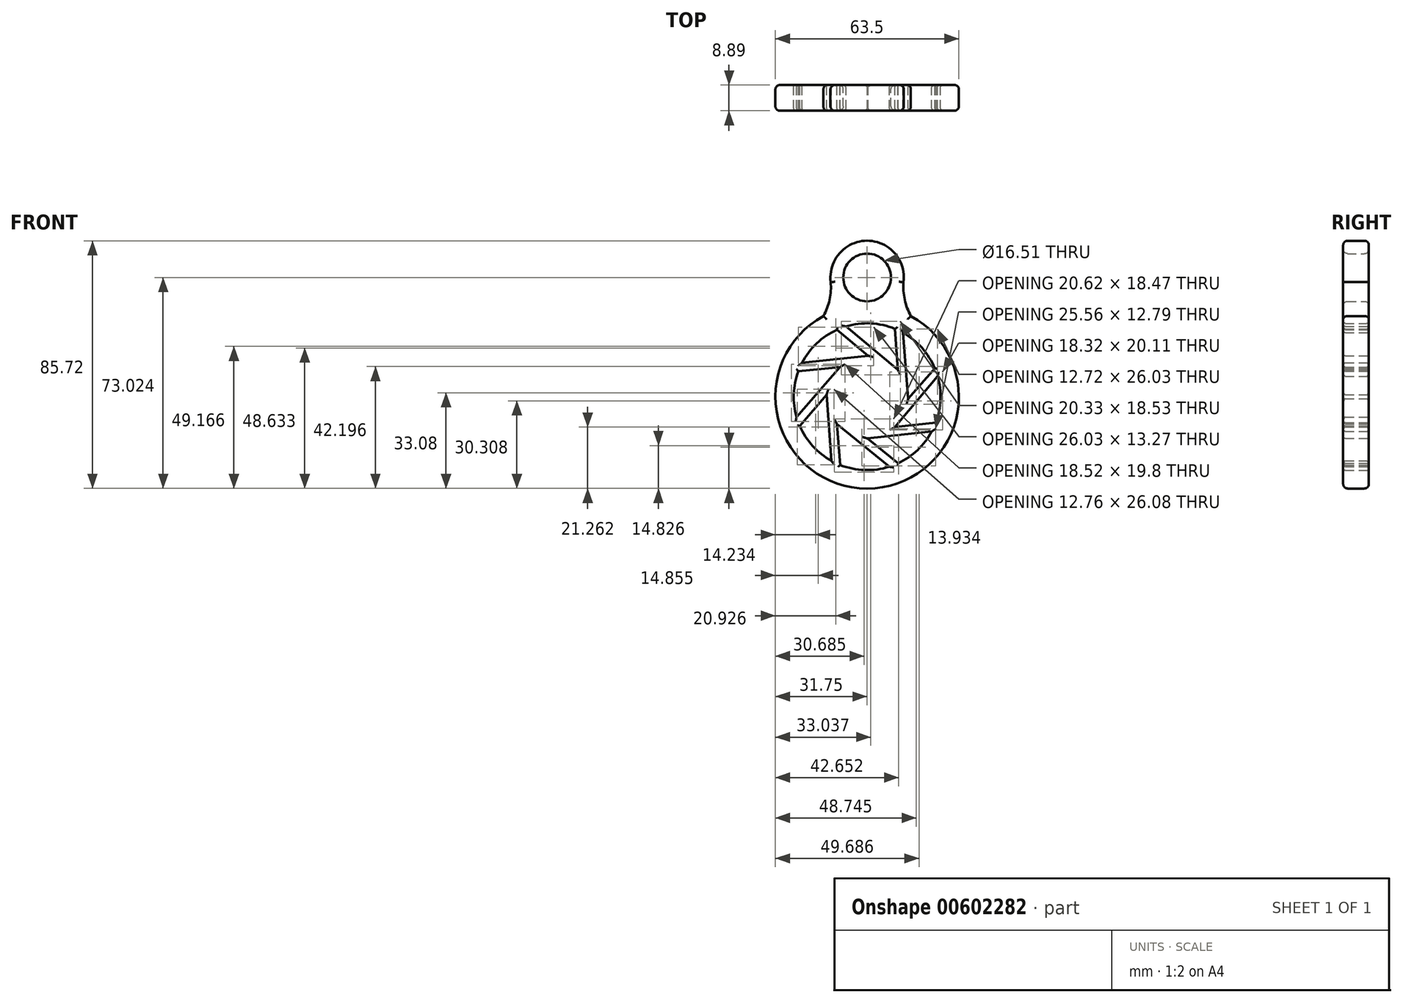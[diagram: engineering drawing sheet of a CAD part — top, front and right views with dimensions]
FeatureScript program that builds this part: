
annotation { "Feature Type Name" : "Feature", "Feature Type Description" : "" }
export const myFeature = defineFeature(function(context is Context, id is Id, definition is map)
    precondition{}
    {
        {
            var Q0;
            Q0=qCreatedBy(makeId("Front.planeOp"),FACE);
            var sketch = newSketch(context, id + "F0", { "sketchPlane" : qUnion([Q0])});
            skArc(sketch, "E0", {"start": v(-15.73, 48.69) * mm, "mid": v(-24.16, 50.57) * mm, "end": v(-32.74, 49.52) * mm});
            skLineSegment(sketch, "E1", {"start": v(-49.23, 34) * mm, "end": v(-34.86, 35.47) * mm});
            skLineSegment(sketch, "E2", {"start": v(-34.86, 35.47) * mm, "end": v(-49.8, 18.16) * mm});
            skLineSegment(sketch, "E3", {"start": v(-48.7, 15.1) * mm, "end": v(-39.45, 25.87) * mm});
            skLineSegment(sketch, "E4", {"start": v(-39.45, 25.87) * mm, "end": v(-37.7, 2.98) * mm});
            skLineSegment(sketch, "E5", {"start": v(-34.68, 1.56) * mm, "end": v(-35.87, 15.8) * mm});
            skLineSegment(sketch, "E6", {"start": v(-35.87, 15.8) * mm, "end": v(-17.7, 1) * mm});
            skLineSegment(sketch, "E7", {"start": v(-14.67, 2.18) * mm, "end": v(-25.36, 10.77) * mm});
            skLineSegment(sketch, "E8", {"start": v(-25.36, 10.77) * mm, "end": v(-3.03, 13.17) * mm});
            skLineSegment(sketch, "E9", {"start": v(-1.6, 16.3) * mm, "end": v(-15.75, 14.68) * mm});
            skLineSegment(sketch, "E10", {"start": v(-15.75, 14.68) * mm, "end": v(-1, 32.26) * mm});
            skLineSegment(sketch, "E11", {"start": v(-1.99, 35.05) * mm, "end": v(-11.16, 24.5) * mm});
            skLineSegment(sketch, "E12", {"start": v(-11.16, 24.5) * mm, "end": v(-12.95, 47.34) * mm});
            skLineSegment(sketch, "E13", {"start": v(-15.73, 48.69) * mm, "end": v(-14.82, 34.54) * mm});
            skLineSegment(sketch, "E14", {"start": v(-14.82, 34.54) * mm, "end": v(-32.74, 49.52) * mm});
            skLineSegment(sketch, "E15", {"start": v(-35.82, 48.36) * mm, "end": v(-25.08, 39.42) * mm});
            skLineSegment(sketch, "E16", {"start": v(-25.08, 39.42) * mm, "end": v(-47.95, 36.9) * mm});
            skArc(sketch, "E17", {"start": v(-40.52, 53.12) * mm, "mid": v(-25.4, -6.55) * mm, "end": v(-10.28, 53.12) * mm});
            skArc(sketch, "E18.trimOffspring", {"start": v(-35.82, 48.36) * mm, "mid": v(-42.85, 43.65) * mm, "end": v(-47.95, 36.9) * mm});
            skArc(sketch, "E19.trimOffspring", {"start": v(-49.23, 34) * mm, "mid": v(-50.78, 26.13) * mm, "end": v(-49.8, 18.16) * mm});
            skArc(sketch, "E20.trimOffspring", {"start": v(-48.7, 15.1) * mm, "mid": v(-44.2, 8.13) * mm, "end": v(-37.7, 2.98) * mm});
            skArc(sketch, "E21.trimOffspring", {"start": v(-34.68, 1.56) * mm, "mid": v(-26.24, -0.19) * mm, "end": v(-17.7, 1) * mm});
            skArc(sketch, "E22.trimOffspring", {"start": v(-14.67, 2.18) * mm, "mid": v(-7.96, 6.73) * mm, "end": v(-3.03, 13.17) * mm});
            skArc(sketch, "E23.trimOffspring", {"start": v(-1.6, 16.3) * mm, "mid": v(-0.02, 24.24) * mm, "end": v(-1, 32.26) * mm});
            skArc(sketch, "E24.trimOffspring", {"start": v(-1.99, 35.05) * mm, "mid": v(-6.45, 42.1) * mm, "end": v(-12.95, 47.34) * mm});
            skLineSegment(sketch, "E25", {"start": v(-25.4, 25.2) * mm, "end": v(-25.4, 76) * mm, "construction": true});
            skLineSegment(sketch, "E26", {"start": v(-25.4, 56.95) * mm, "end": v(-25.4, 76) * mm});
            skArc(sketch, "E27", {"start": v(-12.8, 64.84) * mm, "mid": v(-25.4, 79.17) * mm, "end": v(-38, 64.84) * mm});
            skArc(sketch, "E28", {"start": v(-40.52, 53.12) * mm, "mid": v(-38.4, 58.8) * mm, "end": v(-38, 64.84) * mm});
            skArc(sketch, "E29", {"start": v(-12.8, 64.84) * mm, "mid": v(-12.39, 58.8) * mm, "end": v(-10.28, 53.12) * mm});
            skCircle(sketch, "E30", {"center": v(-25.4, 66.47) * mm, "radius": 8.26 * mm});
            skSolve(sketch);
        }
        {
            var Q0;
            Q0=makeQuery(id+"F0.imprint","IMPRINT",FACE,{"disambiguationData":[TD([[makeQuery(id+"F0.imprint","IMPRINT",EDGE,{"derivedFrom":sQuery(id+"F0.wireOp",EDGE,"E0")}),-1.0]])]});
            extrude(context, id + "F1", {"entities" : qUnion([Q0]), "depth" : 8.9 * mm, "offsetDistance" : 25.4 * mm});
        }
        {
            var Q0;
            Q0=makeQuery(id+"F1.opExtrude","CAP_EDGE",EDGE,{"disambiguationData":[OSD([sQuery(id+"F0.wireOp",EDGE,"E17")])],"isStart":false});
            var Q1;
            Q1=makeQuery(id+"F1.opExtrude","CAP_EDGE",EDGE,{"disambiguationData":[OSD([sQuery(id+"F0.wireOp",EDGE,"E17")])],"isStart":true});
            var Q2;
            Q2=makeQuery(id+"F1.opExtrude","CAP_EDGE",EDGE,{"disambiguationData":[OSD([sQuery(id+"F0.wireOp",EDGE,"E29")])],"isStart":false});
            var Q3;
            Q3=makeQuery(id+"F1.opExtrude","CAP_EDGE",EDGE,{"disambiguationData":[OSD([sQuery(id+"F0.wireOp",EDGE,"E29")])],"isStart":true});
            var Q4;
            Q4=makeQuery(id+"F1.opExtrude","CAP_EDGE",EDGE,{"disambiguationData":[OSD([sQuery(id+"F0.wireOp",EDGE,"E28")])],"isStart":false});
            var Q5;
            Q5=makeQuery(id+"F1.opExtrude","CAP_EDGE",EDGE,{"disambiguationData":[OSD([sQuery(id+"F0.wireOp",EDGE,"E28")])],"isStart":true});
            var Q6;
            Q6=makeQuery(id+"F1.opExtrude","CAP_EDGE",EDGE,{"disambiguationData":[OSD([sQuery(id+"F0.wireOp",EDGE,"E27")])],"isStart":false});
            var Q7;
            Q7=makeQuery(id+"F1.opExtrude","CAP_EDGE",EDGE,{"disambiguationData":[OSD([sQuery(id+"F0.wireOp",EDGE,"E27")])],"isStart":true});
            var Q8;
            Q8=makeQuery(id+"F1.opExtrude","CAP_EDGE",EDGE,{"disambiguationData":[OSD([sQuery(id+"F0.wireOp",EDGE,"E30")])],"isStart":false});
            var Q9;
            Q9=makeQuery(id+"F1.opExtrude","CAP_EDGE",EDGE,{"disambiguationData":[OSD([sQuery(id+"F0.wireOp",EDGE,"E30")])],"isStart":true});
            fillet(context, id + "F2", {"entities" : qUnion([Q0, Q1, Q2, Q3, Q4, Q5, Q6, Q7, Q8, Q9]), "radius" : 1.52 * mm, "tangentPropagation" : true, "allowEdgeOverflow" : false});
        }
        {
            var Q0;
            Q0=makeQuery(id+"F1.opExtrude","CAP_EDGE",EDGE,{"disambiguationData":[OSD([sQuery(id+"F0.wireOp",EDGE,"E20.trimOffspring")])],"isStart":false});
            var Q1;
            Q1=makeQuery(id+"F1.opExtrude","CAP_EDGE",EDGE,{"disambiguationData":[OSD([sQuery(id+"F0.wireOp",EDGE,"E4")])],"isStart":false});
            var Q2;
            Q2=makeQuery(id+"F1.opExtrude","CAP_EDGE",EDGE,{"disambiguationData":[OSD([sQuery(id+"F0.wireOp",EDGE,"E3")])],"isStart":false});
            var Q3;
            Q3=makeQuery(id+"F1.opExtrude","CAP_EDGE",EDGE,{"disambiguationData":[OSD([sQuery(id+"F0.wireOp",EDGE,"E2")])],"isStart":false});
            var Q4;
            Q4=makeQuery(id+"F1.opExtrude","CAP_EDGE",EDGE,{"disambiguationData":[OSD([sQuery(id+"F0.wireOp",EDGE,"E19.trimOffspring")])],"isStart":false});
            var Q5;
            Q5=makeQuery(id+"F1.opExtrude","CAP_EDGE",EDGE,{"disambiguationData":[OSD([sQuery(id+"F0.wireOp",EDGE,"E1")])],"isStart":false});
            var Q6;
            Q6=makeQuery(id+"F1.opExtrude","CAP_EDGE",EDGE,{"disambiguationData":[OSD([sQuery(id+"F0.wireOp",EDGE,"E16")])],"isStart":false});
            var Q7;
            Q7=makeQuery(id+"F1.opExtrude","CAP_EDGE",EDGE,{"disambiguationData":[OSD([sQuery(id+"F0.wireOp",EDGE,"E18.trimOffspring")])],"isStart":false});
            var Q8;
            Q8=makeQuery(id+"F1.opExtrude","CAP_EDGE",EDGE,{"disambiguationData":[OSD([sQuery(id+"F0.wireOp",EDGE,"E15")])],"isStart":false});
            var Q9;
            Q9=makeQuery(id+"F1.opExtrude","CAP_EDGE",EDGE,{"disambiguationData":[OSD([sQuery(id+"F0.wireOp",EDGE,"E0")])],"isStart":false});
            var Q10;
            Q10=makeQuery(id+"F1.opExtrude","CAP_EDGE",EDGE,{"disambiguationData":[OSD([sQuery(id+"F0.wireOp",EDGE,"E14")])],"isStart":false});
            var Q11;
            Q11=makeQuery(id+"F1.opExtrude","CAP_EDGE",EDGE,{"disambiguationData":[OSD([sQuery(id+"F0.wireOp",EDGE,"E13")])],"isStart":false});
            var Q12;
            Q12=makeQuery(id+"F1.opExtrude","CAP_EDGE",EDGE,{"disambiguationData":[OSD([sQuery(id+"F0.wireOp",EDGE,"E12")])],"isStart":false});
            var Q13;
            Q13=makeQuery(id+"F1.opExtrude","CAP_EDGE",EDGE,{"disambiguationData":[OSD([sQuery(id+"F0.wireOp",EDGE,"E24.trimOffspring")])],"isStart":false});
            var Q14;
            Q14=makeQuery(id+"F1.opExtrude","CAP_EDGE",EDGE,{"disambiguationData":[OSD([sQuery(id+"F0.wireOp",EDGE,"E11")])],"isStart":false});
            var Q15;
            Q15=makeQuery(id+"F1.opExtrude","CAP_EDGE",EDGE,{"disambiguationData":[OSD([sQuery(id+"F0.wireOp",EDGE,"E10")])],"isStart":false});
            var Q16;
            Q16=makeQuery(id+"F1.opExtrude","CAP_EDGE",EDGE,{"disambiguationData":[OSD([sQuery(id+"F0.wireOp",EDGE,"E23.trimOffspring")])],"isStart":false});
            var Q17;
            Q17=makeQuery(id+"F1.opExtrude","CAP_EDGE",EDGE,{"disambiguationData":[OSD([sQuery(id+"F0.wireOp",EDGE,"E9")])],"isStart":false});
            var Q18;
            Q18=makeQuery(id+"F1.opExtrude","CAP_EDGE",EDGE,{"disambiguationData":[OSD([sQuery(id+"F0.wireOp",EDGE,"E8")])],"isStart":false});
            var Q19;
            Q19=makeQuery(id+"F1.opExtrude","CAP_EDGE",EDGE,{"disambiguationData":[OSD([sQuery(id+"F0.wireOp",EDGE,"E22.trimOffspring")])],"isStart":false});
            var Q20;
            Q20=makeQuery(id+"F1.opExtrude","CAP_EDGE",EDGE,{"disambiguationData":[OSD([sQuery(id+"F0.wireOp",EDGE,"E7")])],"isStart":false});
            var Q21;
            Q21=makeQuery(id+"F1.opExtrude","CAP_EDGE",EDGE,{"disambiguationData":[OSD([sQuery(id+"F0.wireOp",EDGE,"E21.trimOffspring")])],"isStart":false});
            var Q22;
            Q22=makeQuery(id+"F1.opExtrude","CAP_EDGE",EDGE,{"disambiguationData":[OSD([sQuery(id+"F0.wireOp",EDGE,"E6")])],"isStart":false});
            var Q23;
            Q23=makeQuery(id+"F1.opExtrude","CAP_EDGE",EDGE,{"disambiguationData":[OSD([sQuery(id+"F0.wireOp",EDGE,"E5")])],"isStart":false});
            var Q24;
            Q24=makeQuery(id+"F1.opExtrude","CAP_EDGE",EDGE,{"disambiguationData":[OSD([sQuery(id+"F0.wireOp",EDGE,"E14")])],"isStart":true});
            var Q25;
            Q25=makeQuery(id+"F1.opExtrude","CAP_EDGE",EDGE,{"disambiguationData":[OSD([sQuery(id+"F0.wireOp",EDGE,"E13")])],"isStart":true});
            var Q26;
            Q26=makeQuery(id+"F1.opExtrude","CAP_EDGE",EDGE,{"disambiguationData":[OSD([sQuery(id+"F0.wireOp",EDGE,"E0")])],"isStart":true});
            var Q27;
            Q27=makeQuery(id+"F1.opExtrude","CAP_EDGE",EDGE,{"disambiguationData":[OSD([sQuery(id+"F0.wireOp",EDGE,"E18.trimOffspring")])],"isStart":true});
            var Q28;
            Q28=makeQuery(id+"F1.opExtrude","CAP_EDGE",EDGE,{"disambiguationData":[OSD([sQuery(id+"F0.wireOp",EDGE,"E16")])],"isStart":true});
            var Q29;
            Q29=makeQuery(id+"F1.opExtrude","CAP_EDGE",EDGE,{"disambiguationData":[OSD([sQuery(id+"F0.wireOp",EDGE,"E15")])],"isStart":true});
            var Q30;
            Q30=makeQuery(id+"F1.opExtrude","CAP_EDGE",EDGE,{"disambiguationData":[OSD([sQuery(id+"F0.wireOp",EDGE,"E1")])],"isStart":true});
            var Q31;
            Q31=makeQuery(id+"F1.opExtrude","CAP_EDGE",EDGE,{"disambiguationData":[OSD([sQuery(id+"F0.wireOp",EDGE,"E2")])],"isStart":true});
            var Q32;
            Q32=makeQuery(id+"F1.opExtrude","CAP_EDGE",EDGE,{"disambiguationData":[OSD([sQuery(id+"F0.wireOp",EDGE,"E19.trimOffspring")])],"isStart":true});
            var Q33;
            Q33=makeQuery(id+"F1.opExtrude","CAP_EDGE",EDGE,{"disambiguationData":[OSD([sQuery(id+"F0.wireOp",EDGE,"E20.trimOffspring")])],"isStart":true});
            var Q34;
            Q34=makeQuery(id+"F1.opExtrude","CAP_EDGE",EDGE,{"disambiguationData":[OSD([sQuery(id+"F0.wireOp",EDGE,"E3")])],"isStart":true});
            var Q35;
            Q35=makeQuery(id+"F1.opExtrude","CAP_EDGE",EDGE,{"disambiguationData":[OSD([sQuery(id+"F0.wireOp",EDGE,"E4")])],"isStart":true});
            var Q36;
            Q36=makeQuery(id+"F1.opExtrude","CAP_EDGE",EDGE,{"disambiguationData":[OSD([sQuery(id+"F0.wireOp",EDGE,"E6")])],"isStart":true});
            var Q37;
            Q37=makeQuery(id+"F1.opExtrude","CAP_EDGE",EDGE,{"disambiguationData":[OSD([sQuery(id+"F0.wireOp",EDGE,"E5")])],"isStart":true});
            var Q38;
            Q38=makeQuery(id+"F1.opExtrude","CAP_EDGE",EDGE,{"disambiguationData":[OSD([sQuery(id+"F0.wireOp",EDGE,"E21.trimOffspring")])],"isStart":true});
            var Q39;
            Q39=makeQuery(id+"F1.opExtrude","CAP_EDGE",EDGE,{"disambiguationData":[OSD([sQuery(id+"F0.wireOp",EDGE,"E7")])],"isStart":true});
            var Q40;
            Q40=makeQuery(id+"F1.opExtrude","CAP_EDGE",EDGE,{"disambiguationData":[OSD([sQuery(id+"F0.wireOp",EDGE,"E8")])],"isStart":true});
            var Q41;
            Q41=makeQuery(id+"F1.opExtrude","CAP_EDGE",EDGE,{"disambiguationData":[OSD([sQuery(id+"F0.wireOp",EDGE,"E22.trimOffspring")])],"isStart":true});
            var Q42;
            Q42=makeQuery(id+"F1.opExtrude","CAP_EDGE",EDGE,{"disambiguationData":[OSD([sQuery(id+"F0.wireOp",EDGE,"E9")])],"isStart":true});
            var Q43;
            Q43=makeQuery(id+"F1.opExtrude","CAP_EDGE",EDGE,{"disambiguationData":[OSD([sQuery(id+"F0.wireOp",EDGE,"E10")])],"isStart":true});
            var Q44;
            Q44=makeQuery(id+"F1.opExtrude","CAP_EDGE",EDGE,{"disambiguationData":[OSD([sQuery(id+"F0.wireOp",EDGE,"E23.trimOffspring")])],"isStart":true});
            var Q45;
            Q45=makeQuery(id+"F1.opExtrude","CAP_EDGE",EDGE,{"disambiguationData":[OSD([sQuery(id+"F0.wireOp",EDGE,"E11")])],"isStart":true});
            var Q46;
            Q46=makeQuery(id+"F1.opExtrude","CAP_EDGE",EDGE,{"disambiguationData":[OSD([sQuery(id+"F0.wireOp",EDGE,"E12")])],"isStart":true});
            var Q47;
            Q47=makeQuery(id+"F1.opExtrude","CAP_EDGE",EDGE,{"disambiguationData":[OSD([sQuery(id+"F0.wireOp",EDGE,"E24.trimOffspring")])],"isStart":true});
            fillet(context, id + "F3", {"entities" : qUnion([Q0, Q1, Q2, Q3, Q4, Q5, Q6, Q7, Q8, Q9, Q10, Q11, Q12, Q13, Q14, Q15, Q16, Q17, Q18, Q19, Q20, Q21, Q22, Q23, Q24, Q25, Q26, Q27, Q28, Q29, Q30, Q31, Q32, Q33, Q34, Q35, Q36, Q37, Q38, Q39, Q40, Q41, Q42, Q43, Q44, Q45, Q46, Q47]), "radius" : 0.76 * mm, "tangentPropagation" : true, "allowEdgeOverflow" : false});
        }
    });
